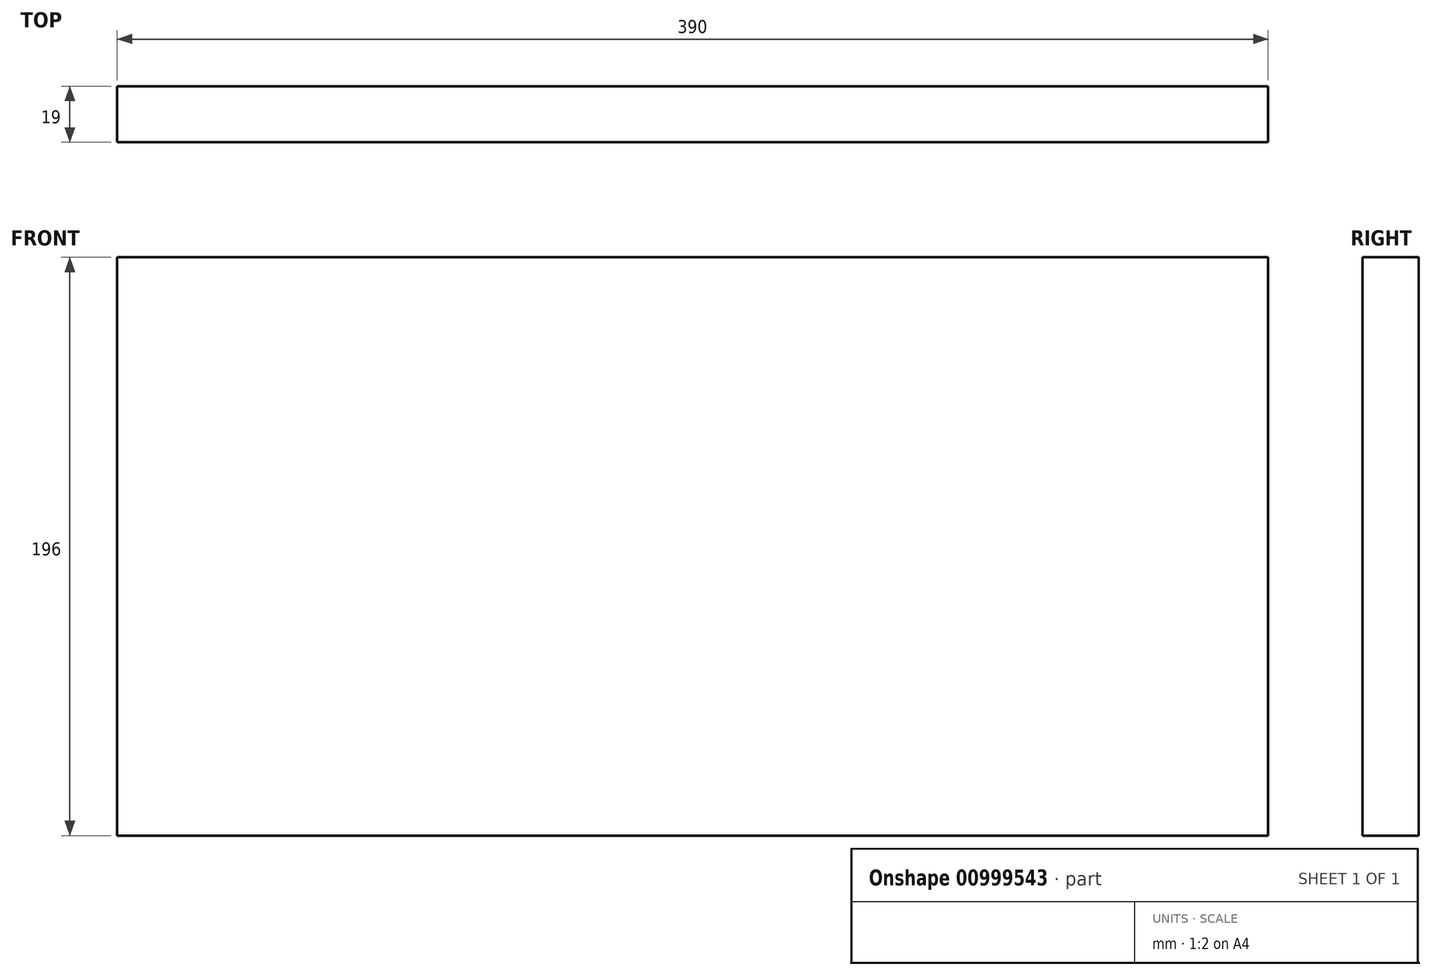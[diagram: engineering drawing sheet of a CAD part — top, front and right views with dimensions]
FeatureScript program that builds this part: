
annotation { "Feature Type Name" : "Feature", "Feature Type Description" : "" }
export const myFeature = defineFeature(function(context is Context, id is Id, definition is map)
    precondition{}
    {
        {
            var Q0;
            Q0=qCreatedBy(makeId("Front.planeOp"),FACE);
            var sketch = newSketch(context, id + "F0", { "sketchPlane" : qUnion([Q0]), "disableImprinting" : false});
            skLineSegment(sketch, "E0.bottom", {"start": v(195, 98) * mm, "end": v(-195, 98) * mm});
            skLineSegment(sketch, "E0.top", {"start": v(195, -98) * mm, "end": v(-195, -98) * mm});
            skLineSegment(sketch, "E0.left", {"start": v(195, 98) * mm, "end": v(195, -98) * mm});
            skLineSegment(sketch, "E0.right", {"start": v(-195, 98) * mm, "end": v(-195, -98) * mm});
            skPoint(sketch, "E0.middle", {"position": v(0, 0) * mm});
            skSolve(sketch);
        }
        {
            var Q0;
            Q0=qSketchRegion(id+"F0",true);
            extrude(context, id + "F1", {"entities" : qUnion([Q0]), "flatOperationType" : FlatOperationType.REMOVE, "thickness1" : 5 * mm, "thickness2" : 0 * mm, "thickness" : 5 * mm, "depth" : 19 * mm, "offsetDistance" : 25 * mm, "startOffsetBound" : StartOffsetType.BLIND, "startOffsetDistance" : 25 * mm, "domain" : OperationDomain.MODEL});
        }
    });
